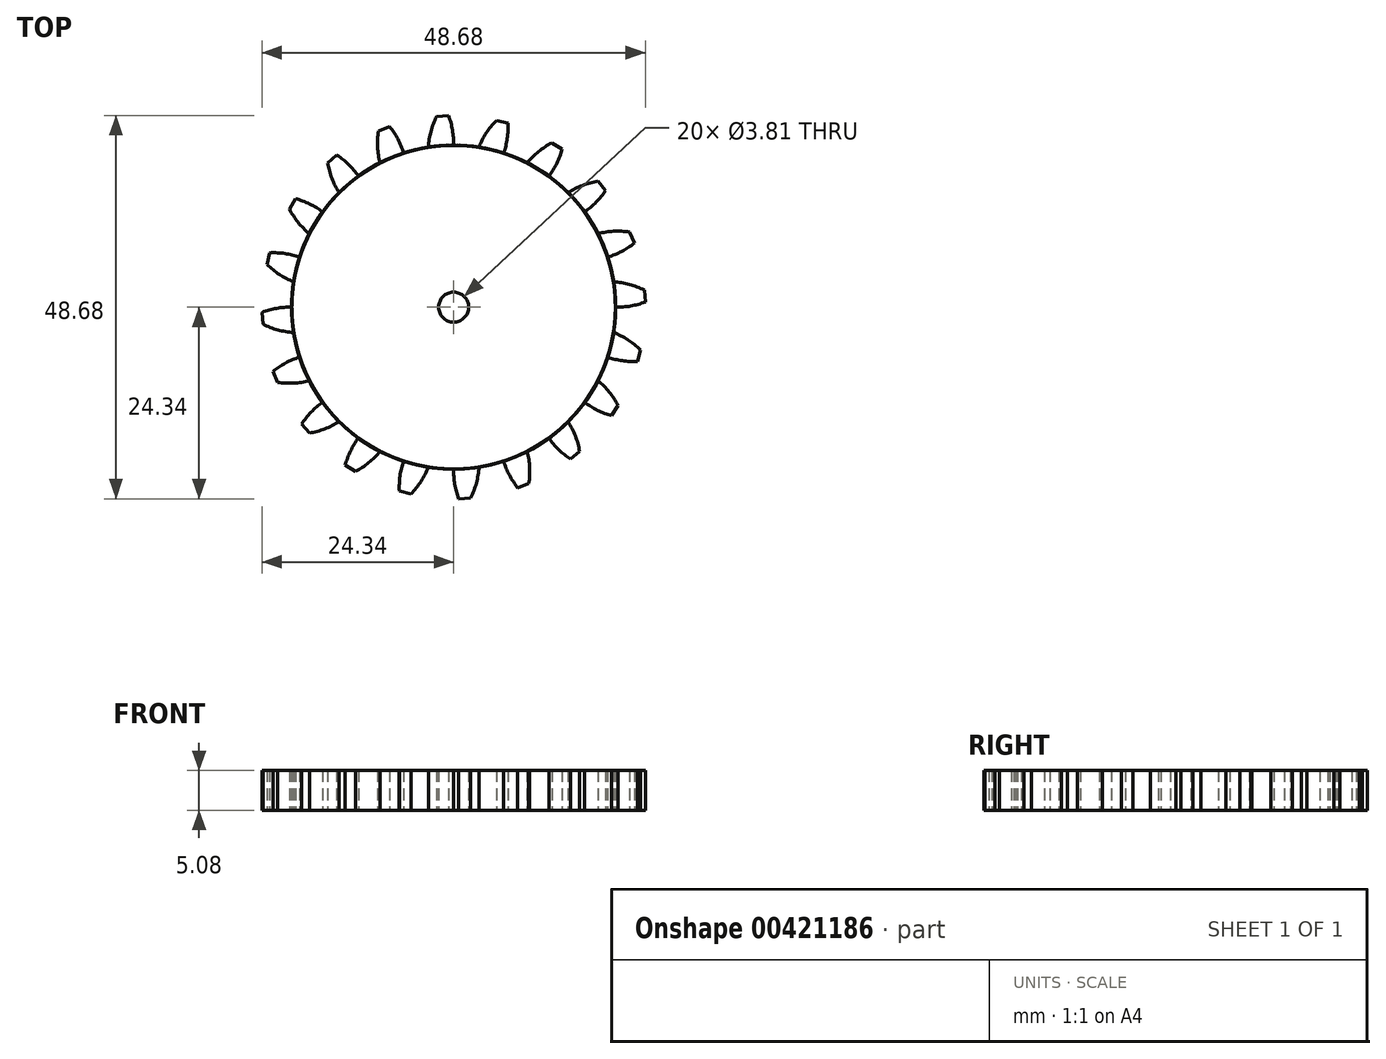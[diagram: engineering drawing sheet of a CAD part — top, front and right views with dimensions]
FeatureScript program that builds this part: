
annotation { "Feature Type Name" : "Feature", "Feature Type Description" : "" }
export const myFeature = defineFeature(function(context is Context, id is Id, definition is map)
    precondition{}
    {
        {
            var Q0;
            Q0=qCreatedBy(makeId("Top.planeOp"),FACE);
            var sketch = newSketch(context, id + "F0", { "sketchPlane" : qUnion([Q0])});
            skCircle(sketch, "E0", {"center": v(0, 0) * mm, "radius": 1.9 * mm});
            skArc(sketch, "E1", {"start": v(20.32, 3.22) * mm, "mid": v(-20.51, -1.61) * mm, "end": v(20.57, 0) * mm});
            skArc(sketch, "E2", {"start": v(24.23, 2.17) * mm, "mid": v(22.33, 2.9) * mm, "end": v(20.32, 3.22) * mm});
            skArc(sketch, "E3", {"start": v(20.57, 0) * mm, "mid": v(22.5, 0.15) * mm, "end": v(24.34, 0.66) * mm});
            skLineSegment(sketch, "E4", {"start": v(24.34, 0.66) * mm, "end": v(24.23, 2.17) * mm});
            skSolve(sketch);
        }
        {
            var Q0;
            Q0=makeQuery(id+"F0.imprint","IMPRINT",FACE,{"disambiguationData":[TD([[makeQuery(id+"F0.imprint","IMPRINT",EDGE,{"derivedFrom":sQuery(id+"F0.wireOp",EDGE,"E0")}),-1.0]])]});
            extrude(context, id + "F1", {"entities" : qUnion([Q0]), "depth" : 5.08 * mm});
        }
        {
            var Q0;
            Q0=makeQuery(id+"F1.opExtrude","SWEPT_BODY",BODY,{"disambiguationData":[OSD([sQuery(id+"F0.wireOp",EDGE,"E0"),sQuery(id+"F0.wireOp",EDGE,"5d23a9fc-8293-4caf-a49c-3b86af3ae94f"),sQuery(id+"F0.wireOp",EDGE,"91eadea3-ba02-48a7-b83c-05411a9213a4"),sQuery(id+"F0.wireOp",EDGE,"ebe4fded-c700-45cb-9476-55bfd9d55064"),sQuery(id+"F0.wireOp",EDGE,"E1")])]});
            var Q1;
            Q1=makeQuery(id+"F1.opExtrude","SWEPT_FACE",FACE,{"disambiguationData":[OSD([sQuery(id+"F0.wireOp",EDGE,"E1")])]});
            circularPattern(context, id + "F2", {"entities" : qUnion([Q0]), "axis" : qUnion([Q1]), "angle" : 360 * degree, "instanceCount" : 20, "oppositeDirection" : true, "equalSpace" : true});
        }
    });
